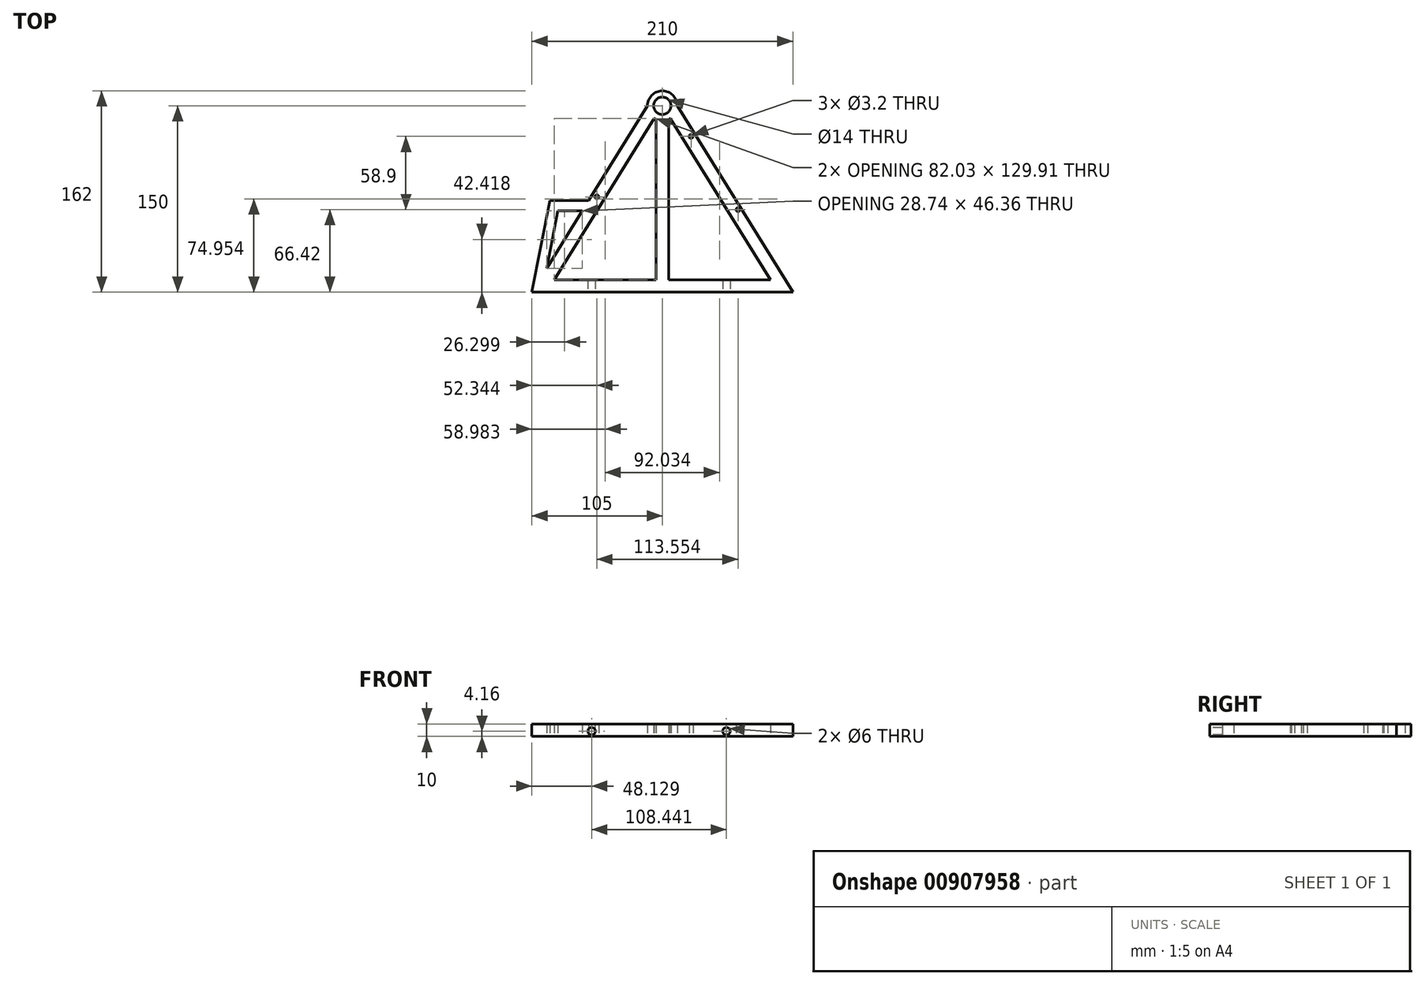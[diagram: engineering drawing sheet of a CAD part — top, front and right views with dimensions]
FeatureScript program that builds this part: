
annotation { "Feature Type Name" : "Feature", "Feature Type Description" : "" }
export const myFeature = defineFeature(function(context is Context, id is Id, definition is map)
    precondition{}
    {
        {
            var Q0;
            Q0=qCreatedBy(makeId("Top.planeOp"),FACE);
            var sketch = newSketch(context, id + "F0", { "sketchPlane" : qUnion([Q0])});
            skCircle(sketch, "E0", {"center": v(0, 0) * mm, "radius": 7 * mm});
            skArc(sketch, "E1", {"start": v(-6.5, -10.1) * mm, "mid": v(-5.76, -10.53) * mm, "end": v(-5, -10.9) * mm});
            skLineSegment(sketch, "E2", {"start": v(0, 0) * mm, "end": v(77.7, 0) * mm, "construction": true});
            skLineSegment(sketch, "E3.0", {"start": v(-105, -150) * mm, "end": v(105, -150) * mm, "construction": true});
            skCircle(sketch, "E4", {"center": v(0, -150) * mm, "radius": 105 * mm, "construction": true});
            skLineSegment(sketch, "E5", {"start": v(-12, 0) * mm, "end": v(-59.37, -76.4) * mm});
            skLineSegment(sketch, "E6", {"start": v(12, 0) * mm, "end": v(105, -150) * mm});
            skLineSegment(sketch, "E7", {"start": v(-105, -150) * mm, "end": v(105, -150) * mm});
            skLineSegment(sketch, "E8.0", {"start": v(-105, -140) * mm, "end": v(-104.52, -140) * mm});
            skLineSegment(sketch, "E9.trimOffspring", {"start": v(-87.03, -140) * mm, "end": v(-5, -140) * mm});
            skLineSegment(sketch, "E10.trimOffspring", {"start": v(104.52, -140) * mm, "end": v(105, -140) * mm});
            skLineSegment(sketch, "E11.trimOffspring", {"start": v(6.5, -10.1) * mm, "end": v(87.03, -140) * mm});
            skLineSegment(sketch, "E12.trimOffspring", {"start": v(-6.5, -10.1) * mm, "end": v(-87.03, -140) * mm});
            skArc(sketch, "E13.trimOffspring", {"start": v(12, 0) * mm, "mid": v(0, 12) * mm, "end": v(-12, 0) * mm});
            skLineSegment(sketch, "E14.trimOffspring", {"start": v(5, -140) * mm, "end": v(87.03, -140) * mm});
            skLineSegment(sketch, "E15.trimOffspring", {"start": v(5, -10.9) * mm, "end": v(5, -140) * mm});
            skLineSegment(sketch, "E16.trimOffspring", {"start": v(-5, -10.9) * mm, "end": v(-5, -140) * mm});
            skArc(sketch, "E17.trimOffspring", {"start": v(5, -10.9) * mm, "mid": v(5.76, -10.53) * mm, "end": v(6.5, -10.1) * mm});
            skLineSegment(sketch, "E18", {"start": v(-105, -150) * mm, "end": v(-90.56, -76.4) * mm});
            skLineSegment(sketch, "E19", {"start": v(-90.56, -76.4) * mm, "end": v(-59.37, -76.4) * mm});
            skLineSegment(sketch, "E20.0", {"start": v(-83.97, -84.4) * mm, "end": v(-64.33, -84.4) * mm});
            skLineSegment(sketch, "E21.trimOffspring", {"start": v(-64.33, -84.4) * mm, "end": v(-93.07, -130.76) * mm});
            skLineSegment(sketch, "E22.trimOffspring", {"start": v(-93.07, -130.76) * mm, "end": v(-83.97, -84.4) * mm});
            skSolve(sketch);
        }
        {
            var Q0;
            Q0 = qSketchRegion(id + "F0", true);
            extrude(context, id + "F1", {"entities" : qUnion([Q0]), "depth" : 10 * mm, "offsetDistance" : 25 * mm});
        }
        {
            var Q0;
            Q0=makeQuery(id+"F1.opExtrude","SWEPT_FACE",FACE,{"disambiguationData":[OSD([sQuery(id+"F0.wireOp",EDGE,"E7")])]});
            var sketch = newSketch(context, id + "F2", { "sketchPlane" : qUnion([Q0])});
            skPoint(sketch, "E23", {"position": v(-56.87, 4.16) * mm});
            skPoint(sketch, "E24", {"position": v(51.57, 4.16) * mm});
            skSolve(sketch);
        }
        {
            var Q0;
            Q0=sQuery(id+"F2.wireOp",VERTEX,"E23");
            var Q1;
            Q1=sQuery(id+"F2.wireOp",VERTEX,"E24");
            var Q2;
            Q2=makeQuery(id+"F1.opExtrude","SWEPT_BODY",BODY,{"disambiguationData":[OSD([sQuery(id+"F0.wireOp",EDGE,"E0"),sQuery(id+"F0.wireOp",EDGE,"E1"),sQuery(id+"F0.wireOp",EDGE,"E5"),sQuery(id+"F0.wireOp",EDGE,"E6"),sQuery(id+"F0.wireOp",EDGE,"E7"),sQuery(id+"F0.wireOp",EDGE,"E9.trimOffspring"),sQuery(id+"F0.wireOp",EDGE,"E11.trimOffspring"),sQuery(id+"F0.wireOp",EDGE,"E12.trimOffspring"),sQuery(id+"F0.wireOp",EDGE,"E13.trimOffspring"),sQuery(id+"F0.wireOp",EDGE,"E14.trimOffspring"),sQuery(id+"F0.wireOp",EDGE,"E15.trimOffspring"),sQuery(id+"F0.wireOp",EDGE,"E16.trimOffspring"),sQuery(id+"F0.wireOp",EDGE,"E17.trimOffspring")])]});
            hole(context, id + "F3", {"style" : HoleStyle.SIMPLE, "endStyle" : HoleEndStyle.BLIND, "holeDiameter" : 6 * mm, "majorDiameter" : 5 * mm, "holeDepth" : 12 * mm, "isTappedThrough" : true, "tappedDepth" : 12 * mm, "tapClearance" : 3, "locations" : qUnion([Q0, Q1]), "scope" : qUnion([Q2])});
        }
        {
            var Q0;
            Q0=qCreatedBy(makeId("Top.planeOp"),FACE);
            var sketch = newSketch(context, id + "F4", { "sketchPlane" : qUnion([Q0])});
            skLineSegment(sketch, "E25.bottom", {"start": v(23.07, -24.68) * mm, "end": v(60.9, -83.58) * mm});
            skLineSegment(sketch, "E25.top", {"start": v(-52.66, -73.31) * mm, "end": v(-14.83, -132.21) * mm});
            skLineSegment(sketch, "E25.left", {"start": v(23.07, -24.68) * mm, "end": v(-52.66, -73.31) * mm});
            skLineSegment(sketch, "E25.right", {"start": v(60.9, -83.58) * mm, "end": v(-14.83, -132.21) * mm});
            skPoint(sketch, "E26", {"position": v(-52.66, -73.31) * mm});
            skPoint(sketch, "E27", {"position": v(23.07, -24.68) * mm});
            skPoint(sketch, "E28", {"position": v(60.9, -83.58) * mm});
            skSolve(sketch);
        }
        {
            var Q0;
            Q0=sQuery(id+"F4.wireOp",VERTEX,"E26");
            var Q1;
            Q1=sQuery(id+"F4.wireOp",VERTEX,"E27");
            var Q2;
            Q2=sQuery(id+"F4.wireOp",VERTEX,"E28");
            var Q3;
            Q3=makeQuery(id+"F1.opExtrude","SWEPT_BODY",BODY,{"disambiguationData":[OSD([sQuery(id+"F0.wireOp",EDGE,"E0"),sQuery(id+"F0.wireOp",EDGE,"E1"),sQuery(id+"F0.wireOp",EDGE,"E5"),sQuery(id+"F0.wireOp",EDGE,"E6"),sQuery(id+"F0.wireOp",EDGE,"E7"),sQuery(id+"F0.wireOp",EDGE,"E9.trimOffspring"),sQuery(id+"F0.wireOp",EDGE,"E11.trimOffspring"),sQuery(id+"F0.wireOp",EDGE,"E12.trimOffspring"),sQuery(id+"F0.wireOp",EDGE,"E13.trimOffspring"),sQuery(id+"F0.wireOp",EDGE,"E14.trimOffspring"),sQuery(id+"F0.wireOp",EDGE,"E15.trimOffspring"),sQuery(id+"F0.wireOp",EDGE,"E16.trimOffspring"),sQuery(id+"F0.wireOp",EDGE,"E17.trimOffspring"),sQuery(id+"F0.wireOp",EDGE,"E18"),sQuery(id+"F0.wireOp",EDGE,"E19"),sQuery(id+"F0.wireOp",EDGE,"E20.0"),sQuery(id+"F0.wireOp",EDGE,"E21.trimOffspring"),sQuery(id+"F0.wireOp",EDGE,"E22.trimOffspring")])]});
            hole(context, id + "F5", {"style" : HoleStyle.SIMPLE, "endStyle" : HoleEndStyle.BLIND, "oppositeDirection" : true, "holeDiameter" : 3.2 * mm, "majorDiameter" : 5 * mm, "holeDepth" : 12 * mm, "isTappedThrough" : true, "tappedDepth" : 12 * mm, "tapClearance" : 3, "locations" : qUnion([Q0, Q1, Q2]), "scope" : qUnion([Q3])});
        }
    });
